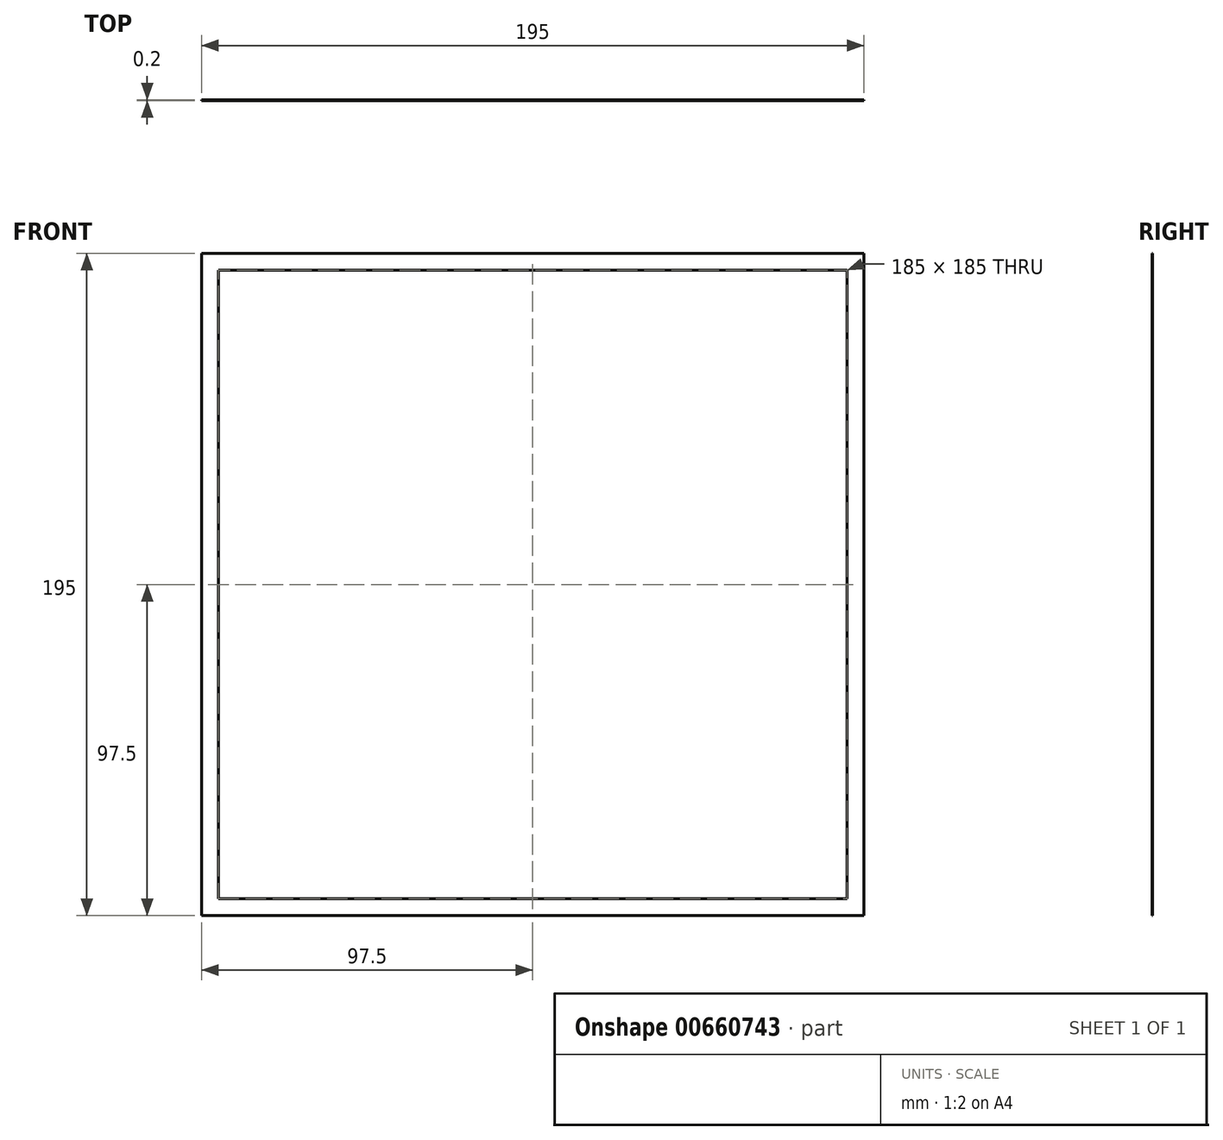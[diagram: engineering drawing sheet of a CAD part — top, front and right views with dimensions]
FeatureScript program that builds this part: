
annotation { "Feature Type Name" : "Feature", "Feature Type Description" : "" }
export const myFeature = defineFeature(function(context is Context, id is Id, definition is map)
    precondition{}
    {
        {
            var Q0;
            Q0=qCreatedBy(makeId("Front.planeOp"),FACE);
            var sketch = newSketch(context, id + "F0", { "sketchPlane" : qUnion([Q0])});
            skLineSegment(sketch, "E0.bottom", {"start": v(97.5, -97.5) * mm, "end": v(-97.5, -97.5) * mm});
            skLineSegment(sketch, "E0.top", {"start": v(97.5, 97.5) * mm, "end": v(-97.5, 97.5) * mm});
            skLineSegment(sketch, "E0.left", {"start": v(97.5, -97.5) * mm, "end": v(97.5, 97.5) * mm});
            skLineSegment(sketch, "E0.right", {"start": v(-97.5, -97.5) * mm, "end": v(-97.5, 97.5) * mm});
            skPoint(sketch, "E0.middle", {"position": v(0, 0) * mm});
            skLineSegment(sketch, "E1.0", {"start": v(-92.5, -92.5) * mm, "end": v(-92.5, 92.5) * mm});
            skLineSegment(sketch, "E1.1", {"start": v(92.5, -92.5) * mm, "end": v(-92.5, -92.5) * mm});
            skLineSegment(sketch, "E1.2", {"start": v(92.5, -92.5) * mm, "end": v(92.5, 92.5) * mm});
            skLineSegment(sketch, "E1.3", {"start": v(92.5, 92.5) * mm, "end": v(-92.5, 92.5) * mm});
            skSolve(sketch);
        }
        {
            var Q0;
            Q0 = qSketchRegion(id + "F0", true);
            extrude(context, id + "F1", {"entities" : qUnion([Q0]), "depth" : .2 * mm, "offsetDistance" : 25 * mm});
        }
    });
